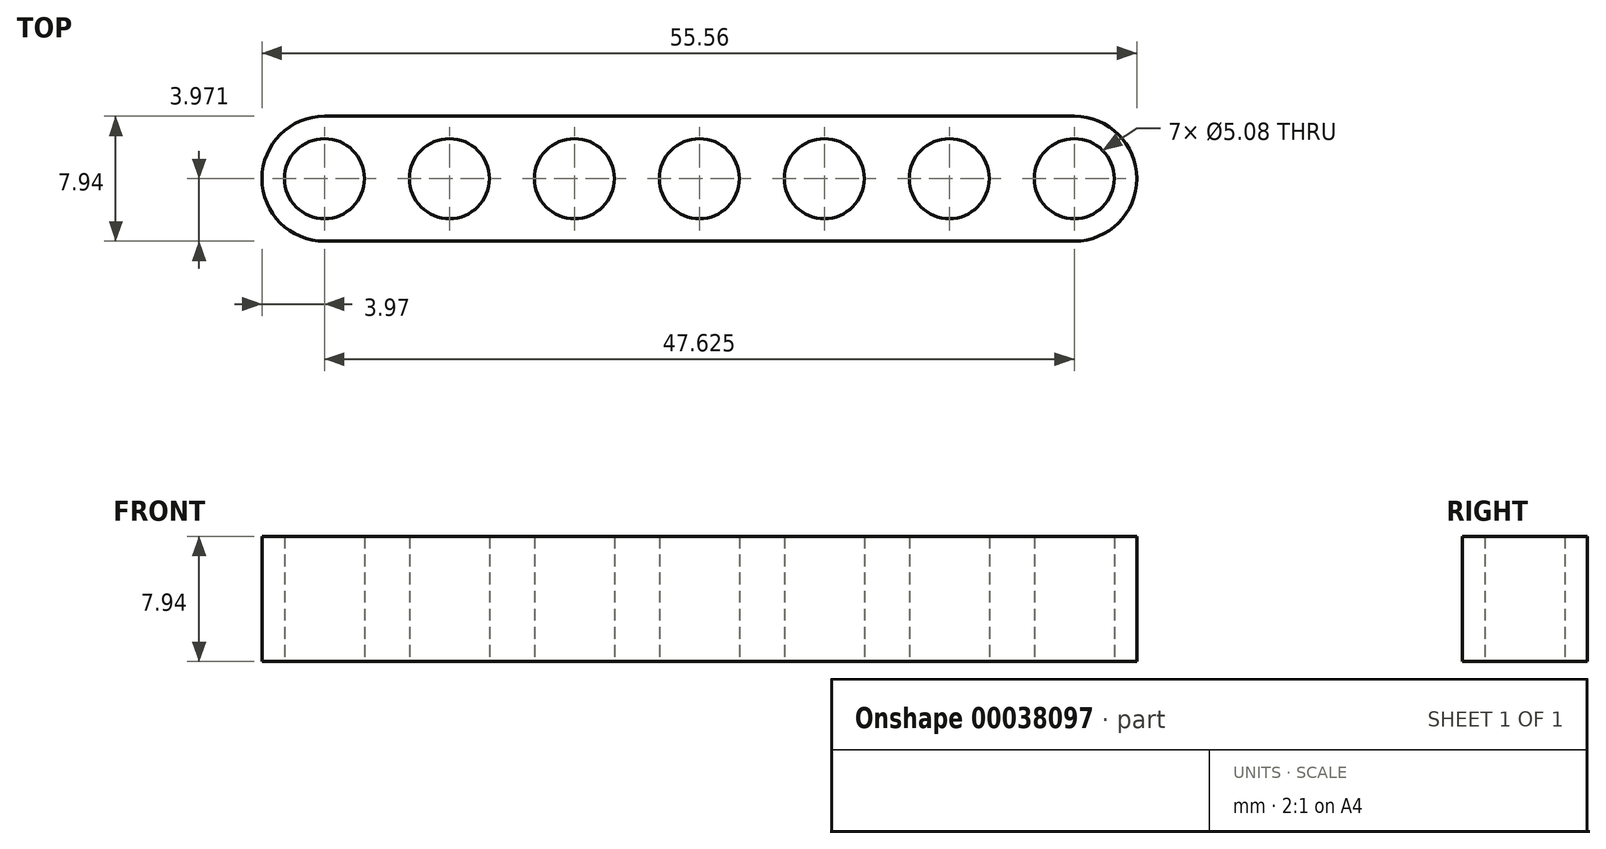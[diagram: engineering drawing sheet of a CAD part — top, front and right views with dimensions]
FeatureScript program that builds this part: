
annotation { "Feature Type Name" : "Feature", "Feature Type Description" : "" }
export const myFeature = defineFeature(function(context is Context, id is Id, definition is map)
    precondition{}
    {
        {
            var Q0;
            Q0=qCreatedBy(makeId("Top.planeOp"),FACE);
            var sketch = newSketch(context, id + "F0", { "sketchPlane" : qUnion([Q0])});
            skLineSegment(sketch, "E0.bottom", {"start": v(0, 0) * mm, "end": v(47.62, 0) * mm});
            skLineSegment(sketch, "E0.top", {"start": v(0, -7.94) * mm, "end": v(47.63, -7.94) * mm});
            skLineSegment(sketch, "E0.left", {"start": v(0, 0) * mm, "end": v(0, -7.94) * mm});
            skLineSegment(sketch, "E0.right", {"start": v(47.63, 0) * mm, "end": v(47.63, -7.94) * mm});
            skLineSegment(sketch, "E1", {"start": v(0, -3.97) * mm, "end": v(7.94, -3.97) * mm, "construction": true});
            skLineSegment(sketch, "E2", {"start": v(7.94, -3.97) * mm, "end": v(15.88, -3.97) * mm, "construction": true});
            skLineSegment(sketch, "E3", {"start": v(15.88, -3.97) * mm, "end": v(23.81, -3.97) * mm, "construction": true});
            skLineSegment(sketch, "E4", {"start": v(23.81, -3.97) * mm, "end": v(31.75, -3.97) * mm, "construction": true});
            skArc(sketch, "E5", {"start": v(0, 0) * mm, "mid": v(-3.97, -3.97) * mm, "end": v(0, -7.94) * mm});
            skCircle(sketch, "E6", {"center": v(0, -3.97) * mm, "radius": 2.54 * mm});
            skCircle(sketch, "E7", {"center": v(7.94, -3.97) * mm, "radius": 2.54 * mm});
            skCircle(sketch, "E8", {"center": v(15.88, -3.97) * mm, "radius": 2.54 * mm});
            skCircle(sketch, "E9", {"center": v(23.81, -3.97) * mm, "radius": 2.54 * mm});
            skCircle(sketch, "E10", {"center": v(31.75, -3.97) * mm, "radius": 2.54 * mm});
            skArc(sketch, "E11", {"start": v(47.63, -7.94) * mm, "mid": v(51.6, -3.97) * mm, "end": v(47.63, 0) * mm});
            skLineSegment(sketch, "E12", {"start": v(31.75, -3.97) * mm, "end": v(39.69, -3.97) * mm, "construction": true});
            skLineSegment(sketch, "E13", {"start": v(39.69, -3.97) * mm, "end": v(47.63, -3.97) * mm, "construction": true});
            skCircle(sketch, "E14", {"center": v(39.69, -3.97) * mm, "radius": 2.54 * mm});
            skCircle(sketch, "E15", {"center": v(47.63, -3.97) * mm, "radius": 2.54 * mm});
            skSolve(sketch);
        }
        {
            var Q0;
            Q0=qSketchRegion(id+"F0",true);
            extrude(context, id + "F1", {"entities" : qUnion([Q0]), "depth" : 7.94 * mm});
        }
    });
